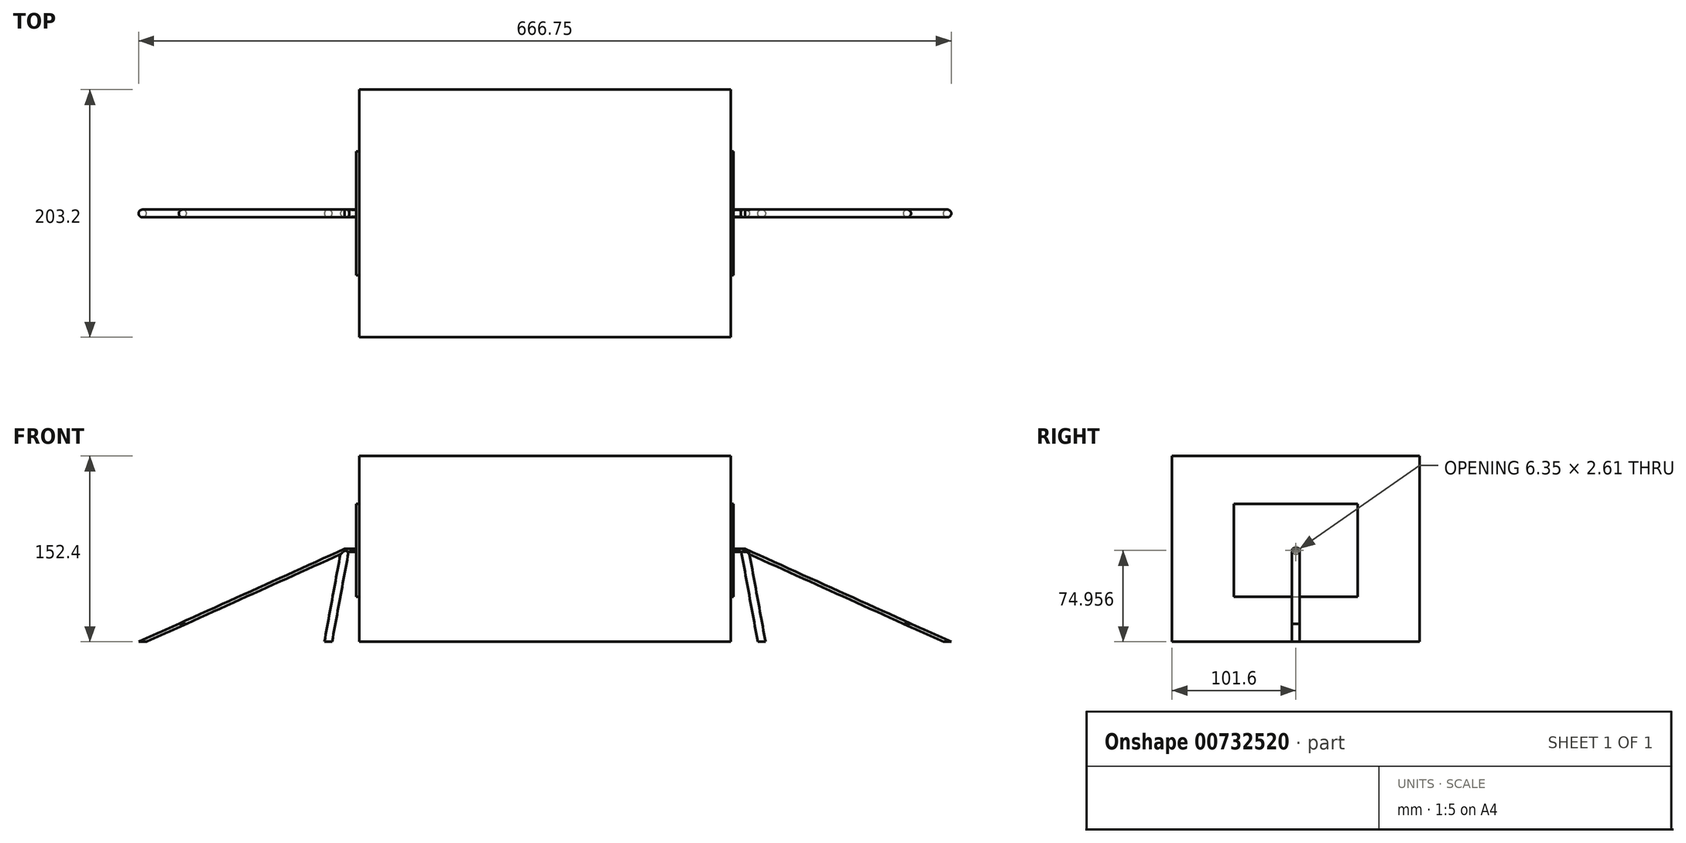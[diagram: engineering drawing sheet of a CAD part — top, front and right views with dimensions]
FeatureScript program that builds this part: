
annotation { "Feature Type Name" : "Feature", "Feature Type Description" : "" }
export const myFeature = defineFeature(function(context is Context, id is Id, definition is map)
    precondition{}
    {
        {
            var Q0;
            Q0=qCreatedBy(makeId("Front.planeOp"),FACE);
            var sketch = newSketch(context, id + "F0", { "sketchPlane" : qUnion([Q0])});
            skLineSegment(sketch, "E0.bottom", {"start": v(-152.4, 0) * mm, "end": v(152.4, 0) * mm});
            skLineSegment(sketch, "E0.top", {"start": v(-152.4, 152.4) * mm, "end": v(152.4, 152.4) * mm});
            skLineSegment(sketch, "E0.left", {"start": v(-152.4, 0) * mm, "end": v(-152.4, 152.4) * mm});
            skLineSegment(sketch, "E0.right", {"start": v(152.4, 0) * mm, "end": v(152.4, 152.4) * mm});
            skSolve(sketch);
        }
        {
            var Q0;
            Q0 = qSketchRegion(id + "F0", true);
            extrude(context, id + "F1", {"entities" : qUnion([Q0]), "depth" : 203.2 * mm, "offsetDistance" : 25.4 * mm, "symmetric" : true});
        }
        {
            var Q0;
            Q0=qCreatedBy(makeId("Front.planeOp"),FACE);
            var sketch = newSketch(context, id + "F2", { "sketchPlane" : qUnion([Q0])});
            skCircle(sketch, "E1", {"center": v(330.2, 0) * mm, "radius": 36.2 * mm});
            skLineSegment(sketch, "E2", {"start": v(330.2, 0) * mm, "end": v(297.21, 14.89) * mm});
            skLineSegment(sketch, "E3", {"start": v(297.21, 14.89) * mm, "end": v(164.09, 74.96) * mm});
            skLineSegment(sketch, "E4", {"start": v(164.09, 74.96) * mm, "end": v(177.8, 0) * mm});
            skLineSegment(sketch, "E5", {"start": v(330.2, 0) * mm, "end": v(-113.7, 0) * mm, "construction": true});
            skCircle(sketch, "E6.MirrorC", {"center": v(-330.2, 0) * mm, "radius": 36.2 * mm});
            skLineSegment(sketch, "E7.MirrorCS", {"start": v(-330.2, 0) * mm, "end": v(-297.21, 14.89) * mm});
            skLineSegment(sketch, "E8.MirrorCS", {"start": v(-164.09, 74.96) * mm, "end": v(-177.8, 0) * mm});
            skLineSegment(sketch, "E9.MirrorCS", {"start": v(-297.21, 14.89) * mm, "end": v(-164.09, 74.96) * mm});
            skLineSegment(sketch, "E10", {"start": v(164.09, 74.96) * mm, "end": v(157.74, 74.96) * mm});
            skLineSegment(sketch, "E11", {"start": v(-164.09, 74.96) * mm, "end": v(-157.74, 74.96) * mm});
            skSolve(sketch);
        }
        {
            var Q0;
            Q0=makeQuery(id+"F1.opExtrude","SWEPT_FACE",FACE,{"disambiguationData":[OSD([sQuery(id+"F0.wireOp",EDGE,"E0.bottom")])]});
            var sketch = newSketch(context, id + "F3", { "sketchPlane" : qUnion([Q0])});
            skPoint(sketch, "E12.0", {"position": v(-177.8, 0) * mm});
            skPoint(sketch, "E13.0", {"position": v(177.8, 0) * mm});
            skCircle(sketch, "E14", {"center": v(177.8, 0) * mm, "radius": 3.18 * mm});
            skCircle(sketch, "E15", {"center": v(-177.8, 0) * mm, "radius": 3.18 * mm});
            skLineSegment(sketch, "E16.0", {"start": v(-164.09, 0) * mm, "end": v(-157.74, 0) * mm});
            skPoint(sketch, "E17.0", {"position": v(-330.2, 0) * mm});
            skCircle(sketch, "E18", {"center": v(-330.2, 0) * mm, "radius": 3.18 * mm});
            skPoint(sketch, "E19.0", {"position": v(330.2, 0) * mm});
            skCircle(sketch, "E20", {"center": v(330.2, 0) * mm, "radius": 3.18 * mm});
            skSolve(sketch);
        }
        {
            var Q0;
            Q0=makeQuery(id+"F3.imprint","IMPRINT",FACE,{"disambiguationData":[TD([[makeQuery(id+"F3.imprint","IMPRINT",EDGE,{"derivedFrom":sQuery(id+"F3.wireOp",EDGE,"E15")}),1.0]])]});
            var Q1;
            Q1=sQuery(id+"F2.wireOp",EDGE,"E8.MirrorCS");
            sweep(context, id + "F4", {"profiles" : qUnion([Q0]), "path" : qUnion([Q1])});
        }
        {
            var Q0;
            Q0=makeQuery(id+"F3.imprint","IMPRINT",FACE,{"disambiguationData":[TD([[makeQuery(id+"F3.imprint","IMPRINT",EDGE,{"derivedFrom":sQuery(id+"F3.wireOp",EDGE,"E14")}),1.0]])]});
            var Q1;
            Q1=sQuery(id+"F2.wireOp",EDGE,"E4");
            sweep(context, id + "F5", {"profiles" : qUnion([Q0]), "path" : qUnion([Q1])});
        }
        {
            var Q0;
            Q0=makeQuery(id+"F3.imprint","IMPRINT",FACE,{"disambiguationData":[TD([[makeQuery(id+"F3.imprint","IMPRINT",EDGE,{"derivedFrom":sQuery(id+"F3.wireOp",EDGE,"E18")}),1.0]])]});
            var Q1;
            Q1=sQuery(id+"F2.wireOp",EDGE,"E7.MirrorCS");
            var Q2;
            Q2=sQuery(id+"F2.wireOp",EDGE,"E9.MirrorCS");
            var Q3;
            Q3=sQuery(id+"F2.wireOp",EDGE,"E11");
            sweep(context, id + "F6", {"operationType" : NewBodyOperationType.ADD, "profiles" : qUnion([Q0]), "path" : qUnion([Q1, Q2, Q3])});
        }
        {
            var Q0;
            Q0=makeQuery(id+"F3.imprint","IMPRINT",FACE,{"disambiguationData":[TD([[makeQuery(id+"F3.imprint","IMPRINT",EDGE,{"derivedFrom":sQuery(id+"F3.wireOp",EDGE,"E20")}),1.0]])]});
            var Q1;
            Q1=sQuery(id+"F2.wireOp",EDGE,"E2");
            var Q2;
            Q2=sQuery(id+"F2.wireOp",EDGE,"E3");
            var Q3;
            Q3=sQuery(id+"F2.wireOp",EDGE,"E10");
            sweep(context, id + "F7", {"operationType" : NewBodyOperationType.ADD, "profiles" : qUnion([Q0]), "path" : qUnion([Q1, Q2, Q3])});
        }
        {
            var Q0;
            Q0=qCreatedBy(makeId("Front.planeOp"),FACE);
            var sketch = newSketch(context, id + "F8", { "sketchPlane" : qUnion([Q0])});
            skLineSegment(sketch, "E21.0", {"start": v(-160.63, 76.26) * mm, "end": v(-154.84, 73.65) * mm});
            skLineSegment(sketch, "E22.0.0", {"start": v(-160.63, 76.26) * mm, "end": v(-154.84, 73.65) * mm, "construction": true});
            skLineSegment(sketch, "E23", {"start": v(-154.84, 73.65) * mm, "end": v(-154.84, 76.26) * mm});
            skLineSegment(sketch, "E24", {"start": v(-154.84, 76.26) * mm, "end": v(-160.63, 76.26) * mm});
            skLineSegment(sketch, "E25.0", {"start": v(154.84, 73.65) * mm, "end": v(160.63, 76.26) * mm});
            skLineSegment(sketch, "E26", {"start": v(154.84, 73.65) * mm, "end": v(154.84, 76.26) * mm});
            skLineSegment(sketch, "E27", {"start": v(154.84, 76.26) * mm, "end": v(160.63, 76.26) * mm});
            skSolve(sketch);
        }
        {
            var Q0;
            Q0 = qSketchRegion(id + "F8", true);
            extrude(context, id + "F9", {"entities" : qUnion([Q0]), "depth" : 6.35 * mm, "offsetDistance" : 25.4 * mm, "symmetric" : true});
        }
        {
            var Q0;
            Q0=makeQuery(id+"F9.opExtrude","SWEPT_FACE",FACE,{"disambiguationData":[OSD([sQuery(id+"F8.wireOp",EDGE,"E23")])]});
            var sketch = newSketch(context, id + "F10", { "sketchPlane" : qUnion([Q0])});
            skPoint(sketch, "E28.0", {"position": v(0, 74.96) * mm});
            skCircle(sketch, "E29", {"center": v(0, 74.96) * mm, "radius": 3.18 * mm});
            skSolve(sketch);
        }
        {
            var Q0;
            {var subQ0=sQuery(id+"F10.wireOp",EDGE,"E29");var subQ1=sQuery(id+"F8.wireOp",EDGE,"E23");var subQ4=makeQuery(id+"F9.opExtrude","CAP_EDGE",EDGE,{"disambiguationData":[OSD([subQ1])],"isStart":true});var subQ5=makeQuery(id+"F10.imprint","INTERSECT",VERTEX,{"derivedFrom":[subQ4,subQ0]});Q0=makeQuery(id+"F10.imprint","IMPRINT",FACE,{"disambiguationData":[TD([[makeQuery(id+"F10.imprint","IMPRINT",EDGE,{"disambiguationData":[TD([[subQ5,-1.0]])],"derivedFrom":subQ0}),-1.0]])]});}
            var Q1;
            {var subQ0=sQuery(id+"F10.wireOp",EDGE,"E29");var subQ1=sQuery(id+"F8.wireOp",EDGE,"E23");var subQ4=makeQuery(id+"F9.opExtrude","CAP_EDGE",EDGE,{"disambiguationData":[OSD([subQ1])],"isStart":false});var subQ5=makeQuery(id+"F10.imprint","INTERSECT",VERTEX,{"derivedFrom":[subQ4,subQ0]});Q1=makeQuery(id+"F10.imprint","IMPRINT",FACE,{"disambiguationData":[TD([[makeQuery(id+"F10.imprint","IMPRINT",EDGE,{"disambiguationData":[TD([[subQ5,1.0]])],"derivedFrom":subQ0}),-1.0]])]});}
            var Q2;
            {var subQ0=sQuery(id+"F10.wireOp",EDGE,"E29");var subQ1=sQuery(id+"F8.wireOp",EDGE,"E23");var subQ2=makeQuery(id+"F9.opExtrude","CAP_EDGE",EDGE,{"disambiguationData":[OSD([subQ1])],"isStart":false});var subQ3=makeQuery(id+"F10.imprint","INTERSECT",VERTEX,{"derivedFrom":[subQ2,subQ0]});Q2=makeQuery(id+"F10.imprint","IMPRINT",FACE,{"disambiguationData":[TD([[makeQuery(id+"F10.imprint","IMPRINT",EDGE,{"disambiguationData":[TD([[subQ3,-1.0]])],"derivedFrom":subQ0}),-1.0]])]});}
            var Q3;
            {var subQ0=sQuery(id+"F10.wireOp",EDGE,"E29");var subQ1=sQuery(id+"F8.wireOp",EDGE,"E23");var subQ2=makeQuery(id+"F9.opExtrude","CAP_EDGE",EDGE,{"disambiguationData":[OSD([subQ1])],"isStart":true});var subQ3=makeQuery(id+"F10.imprint","INTERSECT",VERTEX,{"derivedFrom":[subQ2,subQ0]});Q3=makeQuery(id+"F10.imprint","IMPRINT",FACE,{"disambiguationData":[TD([[makeQuery(id+"F10.imprint","IMPRINT",EDGE,{"disambiguationData":[TD([[subQ3,1.0]])],"derivedFrom":subQ0}),-1.0]])]});}
            extrude(context, id + "F11", {"entities" : qUnion([Q0, Q1, Q2, Q3]), "operationType" : NewBodyOperationType.REMOVE, "oppositeDirection" : true, "depth" : 3.8 * mm, "offsetDistance" : 25.4 * mm});
        }
        {
            var Q0;
            Q0=makeQuery(id+"F9.opExtrude","SWEPT_FACE",FACE,{"disambiguationData":[OSD([sQuery(id+"F8.wireOp",EDGE,"E26")])]});
            var sketch = newSketch(context, id + "F12", { "sketchPlane" : qUnion([Q0])});
            skPoint(sketch, "E30.0", {"position": v(0, 74.96) * mm});
            skCircle(sketch, "E31", {"center": v(0, 74.96) * mm, "radius": 3.18 * mm});
            skSolve(sketch);
        }
        {
            var Q0;
            {var subQ0=sQuery(id+"F12.wireOp",EDGE,"E31");var subQ1=sQuery(id+"F8.wireOp",EDGE,"E26");var subQ4=makeQuery(id+"F9.opExtrude","CAP_EDGE",EDGE,{"disambiguationData":[OSD([subQ1])],"isStart":true});var subQ5=makeQuery(id+"F12.imprint","INTERSECT",VERTEX,{"derivedFrom":[subQ4,subQ0]});Q0=makeQuery(id+"F12.imprint","IMPRINT",FACE,{"disambiguationData":[TD([[makeQuery(id+"F12.imprint","IMPRINT",EDGE,{"disambiguationData":[TD([[subQ5,1.0]])],"derivedFrom":subQ0}),-1.0]])]});}
            var Q1;
            {var subQ0=sQuery(id+"F12.wireOp",EDGE,"E31");var subQ1=sQuery(id+"F8.wireOp",EDGE,"E26");var subQ4=makeQuery(id+"F9.opExtrude","CAP_EDGE",EDGE,{"disambiguationData":[OSD([subQ1])],"isStart":false});var subQ5=makeQuery(id+"F12.imprint","INTERSECT",VERTEX,{"derivedFrom":[subQ4,subQ0]});Q1=makeQuery(id+"F12.imprint","IMPRINT",FACE,{"disambiguationData":[TD([[makeQuery(id+"F12.imprint","IMPRINT",EDGE,{"disambiguationData":[TD([[subQ5,-1.0]])],"derivedFrom":subQ0}),-1.0]])]});}
            var Q2;
            {var subQ0=sQuery(id+"F12.wireOp",EDGE,"E31");var subQ1=sQuery(id+"F8.wireOp",EDGE,"E26");var subQ2=makeQuery(id+"F9.opExtrude","CAP_EDGE",EDGE,{"disambiguationData":[OSD([subQ1])],"isStart":false});var subQ3=makeQuery(id+"F12.imprint","INTERSECT",VERTEX,{"derivedFrom":[subQ2,subQ0]});Q2=makeQuery(id+"F12.imprint","IMPRINT",FACE,{"disambiguationData":[TD([[makeQuery(id+"F12.imprint","IMPRINT",EDGE,{"disambiguationData":[TD([[subQ3,1.0]])],"derivedFrom":subQ0}),-1.0]])]});}
            var Q3;
            {var subQ0=sQuery(id+"F12.wireOp",EDGE,"E31");var subQ1=sQuery(id+"F8.wireOp",EDGE,"E26");var subQ2=makeQuery(id+"F9.opExtrude","CAP_EDGE",EDGE,{"disambiguationData":[OSD([subQ1])],"isStart":true});var subQ3=makeQuery(id+"F12.imprint","INTERSECT",VERTEX,{"derivedFrom":[subQ2,subQ0]});Q3=makeQuery(id+"F12.imprint","IMPRINT",FACE,{"disambiguationData":[TD([[makeQuery(id+"F12.imprint","IMPRINT",EDGE,{"disambiguationData":[TD([[subQ3,-1.0]])],"derivedFrom":subQ0}),-1.0]])]});}
            extrude(context, id + "F13", {"entities" : qUnion([Q0, Q1, Q2, Q3]), "operationType" : NewBodyOperationType.REMOVE, "oppositeDirection" : true, "depth" : 25.4 * mm, "offsetDistance" : 25.4 * mm});
        }
        {
            var Q0;
            Q0=makeQuery(id+"F9.opExtrude","SWEPT_FACE",FACE,{"disambiguationData":[OSD([sQuery(id+"F8.wireOp",EDGE,"E26")])]});
            var sketch = newSketch(context, id + "F14", { "sketchPlane" : qUnion([Q0])});
            skLineSegment(sketch, "E32.0.0", {"start": v(2.9, 76.26) * mm, "end": v(-2.9, 76.26) * mm});
            skArc(sketch, "E32.0.1", {"start": v(-2.9, 76.26) * mm, "mid": v(-3.18, 74.96) * mm, "end": v(-2.9, 73.65) * mm});
            skLineSegment(sketch, "E32.0.2", {"start": v(-2.9, 73.65) * mm, "end": v(2.9, 73.65) * mm});
            skArc(sketch, "E32.0.3", {"start": v(2.9, 73.65) * mm, "mid": v(3.17, 74.96) * mm, "end": v(2.9, 76.26) * mm});
            skLineSegment(sketch, "E33.bottom", {"start": v(50.8, 113.06) * mm, "end": v(-50.8, 113.06) * mm});
            skLineSegment(sketch, "E33.top", {"start": v(50.8, 36.86) * mm, "end": v(-50.8, 36.86) * mm});
            skLineSegment(sketch, "E33.left", {"start": v(50.8, 113.06) * mm, "end": v(50.8, 36.86) * mm});
            skLineSegment(sketch, "E33.right", {"start": v(-50.8, 113.06) * mm, "end": v(-50.8, 36.86) * mm});
            skSolve(sketch);
        }
        {
            var Q0;
            {var subQ0=sQuery(id+"F10.wireOp",EDGE,"E29");var subQ1=sQuery(id+"F8.wireOp",EDGE,"E23");var subQ7=makeQuery(id+"F10.imprint","INTERSECT",VERTEX,{"derivedFrom":[makeQuery(id+"F9.opExtrude","CAP_EDGE",EDGE,{"disambiguationData":[OSD([subQ1])],"isStart":true}),subQ0]});Q0=makeQuery(id+"F10.imprint","IMPRINT",FACE,{"disambiguationData":[TD([[makeQuery(id+"F10.imprint","IMPRINT",EDGE,{"disambiguationData":[TD([[subQ7,-1.0]])],"derivedFrom":subQ0}),1.0]])]});}
            var sketch = newSketch(context, id + "F15", { "sketchPlane" : qUnion([Q0])});
            skPoint(sketch, "E34.0", {"position": v(0, 74.96) * mm});
            skLineSegment(sketch, "E35.bottom", {"start": v(-50.8, 113.06) * mm, "end": v(50.8, 113.06) * mm});
            skLineSegment(sketch, "E35.top", {"start": v(-50.8, 36.86) * mm, "end": v(50.8, 36.86) * mm});
            skLineSegment(sketch, "E35.left", {"start": v(-50.8, 113.06) * mm, "end": v(-50.8, 36.86) * mm});
            skLineSegment(sketch, "E35.right", {"start": v(50.8, 113.06) * mm, "end": v(50.8, 36.86) * mm});
            skSolve(sketch);
        }
        {
            var Q0;
            Q0=makeQuery(id+"F14.imprint","IMPRINT",FACE,{"disambiguationData":[TD([[makeQuery(id+"F14.imprint","IMPRINT",EDGE,{"derivedFrom":sQuery(id+"F14.wireOp",EDGE,"E32.0.0")}),-1.0]])]});
            var Q1;
            {var subQ0=sQuery(id+"F12.wireOp",EDGE,"E31");var subQ1=sQuery(id+"F8.wireOp",EDGE,"E26");var subQ7=makeQuery(id+"F12.imprint","INTERSECT",VERTEX,{"derivedFrom":[makeQuery(id+"F9.opExtrude","CAP_EDGE",EDGE,{"disambiguationData":[OSD([subQ1])],"isStart":false}),subQ0]});Q1=makeQuery(id+"F12.imprint","IMPRINT",FACE,{"disambiguationData":[TD([[makeQuery(id+"F12.imprint","IMPRINT",EDGE,{"disambiguationData":[TD([[subQ7,-1.0]])],"derivedFrom":subQ0}),1.0]])]});}
            extrude(context, id + "F16", {"entities" : qUnion([Q0, Q1]), "operationType" : NewBodyOperationType.ADD, "depth" : 2.54 * mm, "offsetDistance" : 25.4 * mm});
        }
        {
            var Q0;
            {var subQ0=sQuery(id+"F10.wireOp",EDGE,"E29");var subQ1=sQuery(id+"F8.wireOp",EDGE,"E23");var subQ7=makeQuery(id+"F10.imprint","INTERSECT",VERTEX,{"derivedFrom":[makeQuery(id+"F9.opExtrude","CAP_EDGE",EDGE,{"disambiguationData":[OSD([subQ1])],"isStart":true}),subQ0]});Q0=makeQuery(id+"F10.imprint","IMPRINT",FACE,{"disambiguationData":[TD([[makeQuery(id+"F10.imprint","IMPRINT",EDGE,{"disambiguationData":[TD([[subQ7,-1.0]])],"derivedFrom":subQ0}),1.0]])]});}
            var Q1;
            Q1=makeQuery(id+"F15.imprint","IMPRINT",FACE,{"disambiguationData":[TD([[makeQuery(id+"F15.imprint","IMPRINT",EDGE,{"derivedFrom":sQuery(id+"F15.wireOp",EDGE,"E35.bottom")}),-1.0]])]});
            extrude(context, id + "F17", {"entities" : qUnion([Q0, Q1]), "operationType" : NewBodyOperationType.ADD, "depth" : 2.41 * mm, "offsetDistance" : 25.4 * mm});
        }
    });
